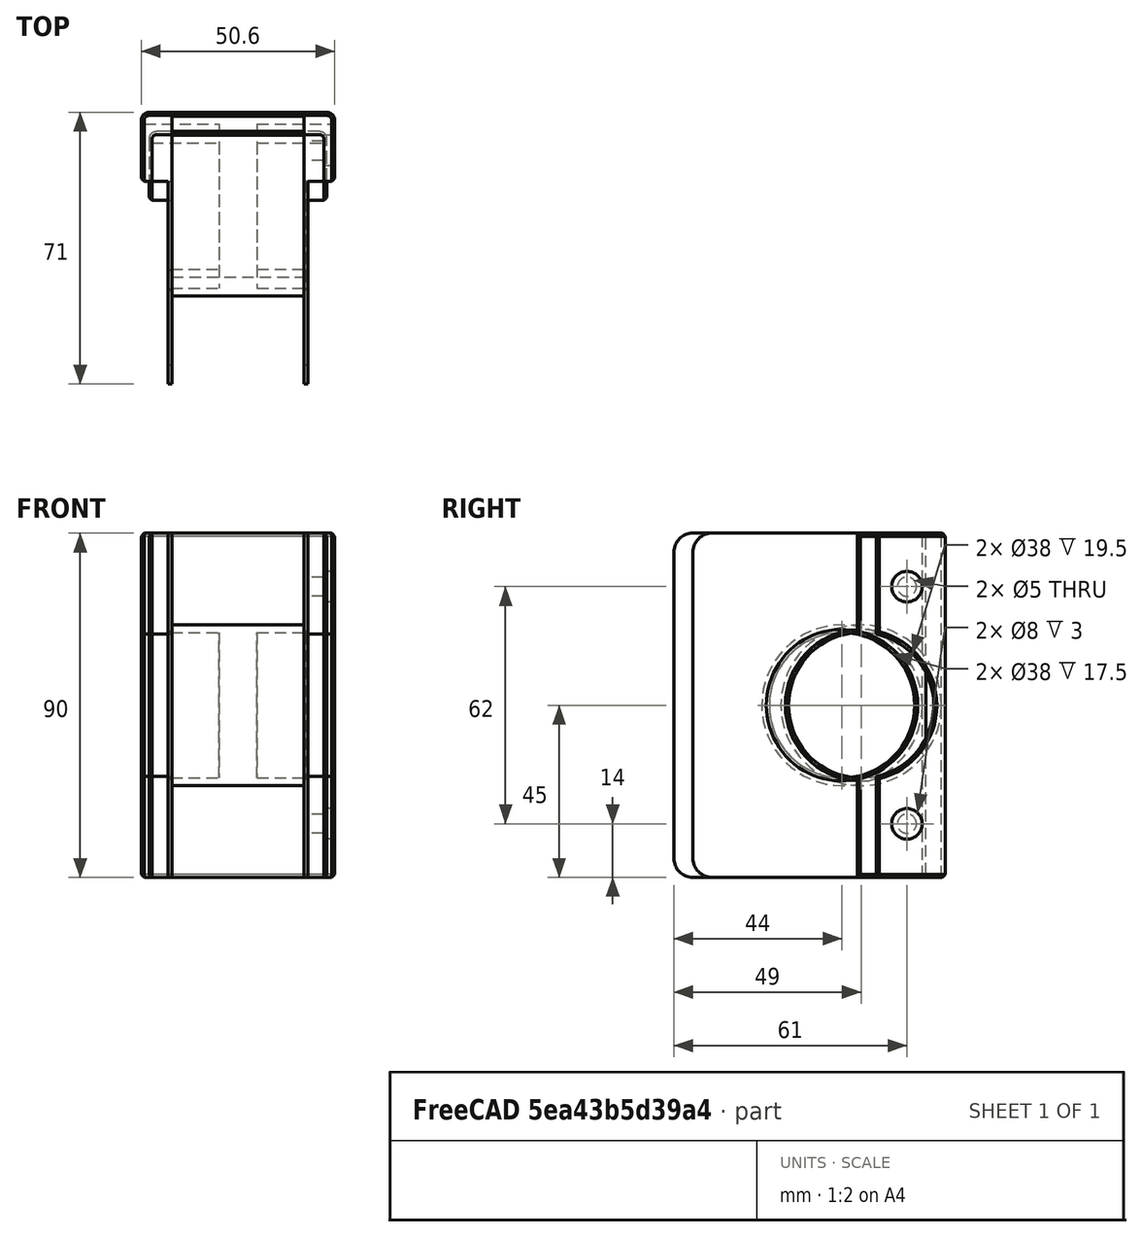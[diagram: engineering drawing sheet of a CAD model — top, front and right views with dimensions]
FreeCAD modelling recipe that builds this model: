
FCSTD DOCUMENT  (FreeCAD 1.1R39315 (Git))
Label: pocket door handle
License: All rights reserved
LicenseURL: http://en.wikipedia.org/wiki/All_rights_reserved
objects: Sketcher::SketchObject×9, PartDesign::Pad×6, PartDesign::Fillet×4, PartDesign::Pocket×3, PartDesign::Chamfer×2, PartDesign::Body×2, PartDesign::Hole×1
note: 68 computed .brp shape members not serialized (recipe doc carries the construction recipe); baked Part::Feature solids carry a one-line shape summary decoded from their .brp

FEATURE [Sketcher::SketchObject] Sketch
  ArcFitTolerance = 0
  AttachmentSupport = -> [XY_Plane]
  FullyConstrained = true
  MakeInternals = false
  MapMode = 5
  sketch-geometry (12):
    g0: LineSegment StartX=-17.3 StartY=-30 StartZ=0 EndX=-17.3 EndY=30 EndZ=0
    g1: LineSegment StartX=-17.3 StartY=30 StartZ=0 EndX=17.3 EndY=30 EndZ=0
    g2: LineSegment StartX=17.3 StartY=30 StartZ=0 EndX=17.3 EndY=-30 EndZ=0
    g3: LineSegment StartX=17.3 StartY=-30 StartZ=0 EndX=18.3 EndY=-30 EndZ=0
    g4: LineSegment StartX=18.3 StartY=-30 StartZ=0 EndX=18.3 EndY=13 EndZ=0
    g5: LineSegment StartX=18.3 StartY=13 StartZ=0 EndX=23.3 EndY=13 EndZ=0
    g6: LineSegment StartX=23.3 StartY=13 StartZ=0 EndX=23.3 EndY=31 EndZ=0
    g7: LineSegment StartX=23.3 StartY=31 StartZ=0 EndX=-23.3 EndY=31 EndZ=0
    g8: LineSegment StartX=-23.3 StartY=31 StartZ=0 EndX=-23.3 EndY=13 EndZ=0
    g9: LineSegment StartX=-23.3 StartY=13 StartZ=0 EndX=-18.3 EndY=13 EndZ=0
    g10: LineSegment StartX=-18.3 StartY=13 StartZ=0 EndX=-18.3 EndY=-30 EndZ=0
    g11: LineSegment StartX=-18.3 StartY=-30 StartZ=0 EndX=-17.3 EndY=-30 EndZ=0
  constraints (34):
    c: Vertical(g0)
    c: Coincident(g0,g1)
    c: Horizontal(g1)
    c: Coincident(g1,g2)
    c: Coincident(g2,g3)
    c: Horizontal(g3)
    c: Coincident(g3,g4)
    c: Vertical(g4)
    c: Coincident(g4,g5)
    c: Horizontal(g5)
    c: Coincident(g5,g6)
    c: Vertical(g6)
    c: Coincident(g6,g7)
    c: Horizontal(g7)
    c: Coincident(g7,g8)
    c: Vertical(g8)
    c: Coincident(g8,g9)
    c: Horizontal(g9)
    c: Coincident(g9,g10)
    c: Vertical(g10)
    c: Coincident(g10,g11)
    c: Coincident(g11,g0)
    c: Horizontal(g11)
    c: Symmetric(g2,g0,g-2)
    c: Equal(g11,g3)
    c: Equal(g9,g5)
    c: Equal(g6,g8)
    c: DistanceY(g0,g7) = 1
    c: DistanceX(g9,g0) = 1
    c: DistanceY(g8,g8) = 18
    c: Symmetric(g0,g1,g-1)
    c: DistanceX(g1,g1) = 34.6
    c: DistanceY(g2,g2) = 60
    c: DistanceX(g9,g9) = 5
FEATURE [PartDesign::Pad] Pad
  Direction = (0,0,1)
  Length = 90
  Length2 = 10
  Profile = -> Sketch
  ReferenceAxis = -> Sketch [N_Axis]
  Suppressed = false
  Type = 0
FEATURE [Sketcher::SketchObject] Sketch001
  ArcFitTolerance = 0
  AttachmentSupport = -> [Pad]
  ExternalGeometry = -> [Pad]
  FullyConstrained = true
  MakeInternals = false
  MapMode = 5
  Placement = pos=(23.3,0,0) rot=(0.57735,0.57735,0.57735;2.0944rad)
  sketch-geometry (3):
    g0: Circle CenterX=9 CenterY=45 CenterZ=0 NormalX=0 NormalY=0 NormalZ=1 AngleXU=0 Radius=19
    g1: GeomPoint X=31 Y=45 Z=0
    g2: Circle CenterX=9 CenterY=45 CenterZ=0 NormalX=0 NormalY=0 NormalZ=1 AngleXU=0 Radius=21
  constraints (6):
    c: Diameter(g0) = 38
    c: DistanceX(g0,g-3) = 22
    c: Symmetric(g-3,g-3,g1)
    c: Horizontal(g0,g1)
    c: Coincident(g2,g0)
    c: Diameter(g2) = 42
FEATURE [PartDesign::Pocket] Pocket
  BaseFeature = -> Pad
  Direction = (-1,0,0)
  Length = 5
  Length2 = 5
  Profile = -> Sketch001 [Edge1]
  ReferenceAxis = -> Sketch001 [N_Axis]
  Suppressed = false
  Type = 1
FEATURE [Sketcher::SketchObject] Sketch002
  ArcFitTolerance = 0
  AttachmentSupport = -> [Pocket]
  ExternalGeometry = -> [Sketch001]
  FullyConstrained = true
  MakeInternals = false
  MapMode = 5
  Placement = pos=(18.3,0,0) rot=(0.57735,0.57735,0.57735;2.0944rad)
  sketch-geometry (2):
    g0: Circle CenterX=9 CenterY=45 CenterZ=0 NormalX=0 NormalY=0 NormalZ=1 AngleXU=0 Radius=19
    g1: Circle CenterX=9 CenterY=45 CenterZ=0 NormalX=0 NormalY=0 NormalZ=1 AngleXU=0 Radius=21
  constraints (4):
    c: Coincident(g0,g-4)
    c: Coincident(g1,g0)
    c: Equal(g1,g-4)
    c: Equal(g0,g-3)
FEATURE [PartDesign::Fillet] Fillet
  Base = -> Pocket [Edge46,Edge50]
  BaseFeature = -> Pocket
  Radius = 2
  SupportTransform = false
  Suppressed = false
  UseAllEdges = false
FEATURE [PartDesign::Pad] Pad001
  BaseFeature = -> Fillet
  Direction = (1,0,0)
  Length = 10
  Length2 = 10
  Profile = -> Sketch002
  ReferenceAxis = -> Sketch002 [N_Axis]
  Reversed = true
  Suppressed = false
  Type = 3
  UpToFace = -> Fillet [Face13]
FEATURE [Sketcher::SketchObject] Sketch003
  ArcFitTolerance = 0
  AttachmentSupport = -> [YZ_Plane]
  ExternalGeometry = -> [Pad001]
  FullyConstrained = true
  MakeInternals = false
  MapMode = 5
  Placement = pos=(0,0,0) rot=(0.57735,0.57735,0.57735;2.0944rad)
  sketch-geometry (1):
    g0: Circle CenterX=9 CenterY=45 CenterZ=0 NormalX=0 NormalY=0 NormalZ=1 AngleXU=0 Radius=21
  constraints (2):
    c: Coincident(g0,g-3)
    c: PointOnObject(g-3,g0)
FEATURE [PartDesign::Pad] Pad002
  BaseFeature = -> Pad001
  Direction = (1,0,0)
  Length = 10
  Length2 = 10
  Midplane = true
  Profile = -> Sketch003
  ReferenceAxis = -> Sketch003 [N_Axis]
  Refine = true
  Suppressed = false
  Type = 0
FEATURE [PartDesign::Chamfer] Chamfer
  Angle = 45
  Base = -> Pad002 [Edge36,Edge60,Edge8,Edge32,Edge35,Edge33,Edge18,Edge59,Edge19,Edge17,Edge1,Edge16]
  BaseFeature = -> Pad002
  ChamferType = 0
  FlipDirection = false
  Size = 0.8
  Size2 = 1
  SupportTransform = false
  Suppressed = false
  UseAllEdges = false
FEATURE [PartDesign::Fillet] Fillet001
  Base = -> Chamfer [Edge30,Edge53,Edge5,Edge13]
  BaseFeature = -> Chamfer
  Radius = 5
  SupportTransform = false
  Suppressed = false
  UseAllEdges = false
FEATURE [PartDesign::Body] Body
  AllowCompound = false
  Group = -> [Sketch,Pad,Sketch001,Pocket,Sketch002,Fillet,Pad001,Sketch003,Pad002,Chamfer,Fillet001]
  Origin = -> Origin
  Tip = -> Fillet001
FEATURE [Sketcher::SketchObject] Sketch004
  ArcFitTolerance = 0
  AttachmentSupport = -> [XY_Plane001]
  FullyConstrained = true
  MakeInternals = false
  MapMode = 5
  sketch-geometry (12):
    g0: LineSegment StartX=-17.3 StartY=-35 StartZ=0 EndX=-17.3 EndY=35 EndZ=0
    g1: LineSegment StartX=-17.3 StartY=35 StartZ=0 EndX=17.3 EndY=35 EndZ=0
    g2: LineSegment StartX=17.3 StartY=35 StartZ=0 EndX=17.3 EndY=-35 EndZ=0
    g3: LineSegment StartX=17.3 StartY=-35 StartZ=0 EndX=18.3 EndY=-35 EndZ=0
    g4: LineSegment StartX=18.3 StartY=-35 StartZ=0 EndX=18.3 EndY=18 EndZ=0
    g5: LineSegment StartX=18.3 StartY=18 StartZ=0 EndX=25.3 EndY=18 EndZ=0
    g6: LineSegment StartX=25.3 StartY=18 StartZ=0 EndX=25.3 EndY=36 EndZ=0
    g7: LineSegment StartX=25.3 StartY=36 StartZ=0 EndX=-25.3 EndY=36 EndZ=0
    g8: LineSegment StartX=-25.3 StartY=36 StartZ=0 EndX=-25.3 EndY=18 EndZ=0
    g9: LineSegment StartX=-25.3 StartY=18 StartZ=0 EndX=-18.3 EndY=18 EndZ=0
    g10: LineSegment StartX=-18.3 StartY=18 StartZ=0 EndX=-18.3 EndY=-35 EndZ=0
    g11: LineSegment StartX=-18.3 StartY=-35 StartZ=0 EndX=-17.3 EndY=-35 EndZ=0
  constraints (34):
    c: Vertical(g0)
    c: Coincident(g0,g1)
    c: Horizontal(g1)
    c: Coincident(g1,g2)
    c: Coincident(g2,g3)
    c: Horizontal(g3)
    c: Coincident(g3,g4)
    c: Vertical(g4)
    c: Coincident(g4,g5)
    c: Horizontal(g5)
    c: Coincident(g5,g6)
    c: Vertical(g6)
    c: Coincident(g6,g7)
    c: Horizontal(g7)
    c: Coincident(g7,g8)
    c: Vertical(g8)
    c: Coincident(g8,g9)
    c: Horizontal(g9)
    c: Coincident(g9,g10)
    c: Vertical(g10)
    c: Coincident(g10,g11)
    c: Coincident(g11,g0)
    c: Horizontal(g11)
    c: Symmetric(g2,g0,g-2)
    c: Equal(g11,g3)
    c: Equal(g9,g5)
    c: Equal(g6,g8)
    c: DistanceY(g0,g7) = 1
    c: DistanceX(g9,g0) = 1
    c: DistanceY(g8,g8) = 18
    c: Symmetric(g0,g1,g-1)
    c: DistanceX(g1,g1) = 34.6
    c: DistanceY(g2,g2) = 70
    c: DistanceX(g9,g9) = 7
FEATURE [PartDesign::Pad] Pad003
  Direction = (0,0,1)
  Length = 90
  Length2 = 10
  Profile = -> Sketch004
  ReferenceAxis = -> Sketch004 [N_Axis]
  Suppressed = false
  Type = 0
FEATURE [Sketcher::SketchObject] Sketch005
  ArcFitTolerance = 0
  AttachmentSupport = -> [Pad003]
  ExternalGeometry = -> [Pad003]
  FullyConstrained = true
  MakeInternals = false
  MapMode = 5
  Placement = pos=(25.3,0,0) rot=(0.57735,0.57735,0.57735;2.0944rad)
  sketch-geometry (3):
    g0: Circle CenterX=14 CenterY=45 CenterZ=0 NormalX=0 NormalY=0 NormalZ=1 AngleXU=0 Radius=19
    g1: GeomPoint X=36 Y=45 Z=0
    g2: Circle CenterX=14 CenterY=45 CenterZ=0 NormalX=0 NormalY=0 NormalZ=1 AngleXU=0 Radius=21
  constraints (6):
    c: Diameter(g0) = 38
    c: DistanceX(g0,g-3) = 22
    c: Symmetric(g-3,g-3,g1)
    c: Horizontal(g0,g1)
    c: Coincident(g2,g0)
    c: Diameter(g2) = 42
FEATURE [PartDesign::Pocket] Pocket001
  BaseFeature = -> Pad003
  Direction = (-1,0,0)
  Length = 5
  Length2 = 5
  Profile = -> Sketch005 [Edge1]
  ReferenceAxis = -> Sketch005 [N_Axis]
  Suppressed = false
  Type = 1
FEATURE [PartDesign::Fillet] Fillet002
  Base = -> Pocket001 [Edge46,Edge50]
  BaseFeature = -> Pocket001
  Radius = 2
  SupportTransform = false
  Suppressed = false
  UseAllEdges = false
FEATURE [Sketcher::SketchObject] Sketch006
  ArcFitTolerance = 0
  AttachmentSupport = -> [Pocket001]
  ExternalGeometry = -> [Sketch005]
  FullyConstrained = true
  MakeInternals = false
  MapMode = 5
  Placement = pos=(18.3,0,0) rot=(0.57735,0.57735,0.57735;2.0944rad)
  sketch-geometry (2):
    g0: Circle CenterX=14 CenterY=45 CenterZ=0 NormalX=0 NormalY=0 NormalZ=1 AngleXU=0 Radius=19
    g1: Circle CenterX=14 CenterY=45 CenterZ=0 NormalX=0 NormalY=0 NormalZ=1 AngleXU=0 Radius=21
  constraints (4):
    c: Coincident(g0,g-4)
    c: Coincident(g1,g0)
    c: Equal(g1,g-4)
    c: Equal(g0,g-3)
FEATURE [PartDesign::Pad] Pad004
  BaseFeature = -> Fillet002
  Direction = (1,0,0)
  Length = 10
  Length2 = 10
  Profile = -> Sketch006
  ReferenceAxis = -> Sketch006 [N_Axis]
  Reversed = true
  Suppressed = false
  Type = 3
  UpToFace = -> Fillet002 [Face13]
FEATURE [Sketcher::SketchObject] Sketch007
  ArcFitTolerance = 0
  AttachmentSupport = -> [YZ_Plane001]
  ExternalGeometry = -> [Pad004]
  FullyConstrained = true
  MakeInternals = false
  MapMode = 5
  Placement = pos=(0,0,0) rot=(0.57735,0.57735,0.57735;2.0944rad)
  sketch-geometry (1):
    g0: Circle CenterX=14 CenterY=45 CenterZ=0 NormalX=0 NormalY=0 NormalZ=1 AngleXU=0 Radius=21
  constraints (2):
    c: Coincident(g0,g-3)
    c: PointOnObject(g-3,g0)
FEATURE [PartDesign::Pad] Pad005
  BaseFeature = -> Pad004
  Direction = (1,0,0)
  Length = 10
  Length2 = 10
  Midplane = true
  Profile = -> Sketch007
  ReferenceAxis = -> Sketch007 [N_Axis]
  Refine = true
  Suppressed = false
  Type = 0
FEATURE [PartDesign::Chamfer] Chamfer001
  Angle = 45
  Base = -> Pad005 [Edge36,Edge60,Edge8,Edge32,Edge35,Edge33,Edge18,Edge59,Edge19,Edge17,Edge1,Edge16]
  BaseFeature = -> Pad005
  ChamferType = 0
  FlipDirection = false
  Size = 0.8
  Size2 = 1
  SupportTransform = false
  Suppressed = false
  UseAllEdges = false
FEATURE [PartDesign::Fillet] Fillet003
  Base = -> Chamfer001 [Edge30,Edge53,Edge5,Edge13]
  BaseFeature = -> Chamfer001
  Radius = 5
  SupportTransform = false
  Suppressed = false
  UseAllEdges = false
FEATURE [Sketcher::SketchObject] Sketch008
  ArcFitTolerance = 1e-06
  AttachmentSupport = -> [Fillet003]
  ExternalGeometry = -> [Fillet003]
  FullyConstrained = true
  MakeInternals = false
  MapMode = 5
  Placement = pos=(25.3,0,0) rot=(0.57735,0.57735,0.57735;2.0944rad)
  sketch-geometry (4):
    g0: GeomPoint [constr] X=26 Y=0 Z=0
    g1: GeomPoint [constr] X=26 Y=90 Z=0
    g2: Circle CenterX=26 CenterY=76 CenterZ=0 NormalX=0 NormalY=0 NormalZ=1 AngleXU=0 Radius=2
    g3: Circle CenterX=26 CenterY=14 CenterZ=0 NormalX=0 NormalY=0 NormalZ=1 AngleXU=0 Radius=2
  constraints (8):
    c: Symmetric(g-4,g-4,g0)
    c: Symmetric(g-3,g-3,g1)
    c: Vertical(g0,g3)
    c: Vertical(g2,g3)
    c: DistanceY(g-4,g3) = 14
    c: DistanceY(g2,g-3) = 14
    c: Equal(g2,g3)
    c: Diameter(g2) = 4
FEATURE [PartDesign::Pocket] Pocket002
  BaseFeature = -> Fillet003
  Direction = (-1,0,0)
  Length = 0
  Length2 = 5
  Profile = -> Sketch008
  ReferenceAxis = -> Sketch008 [N_Axis]
  Refine = true
  Suppressed = false
  Type = 3
  UpToFace = -> Fillet003 [Face5]
FEATURE [PartDesign::Hole] Hole
  BaseFeature = -> Pocket002
  CustomThreadClearance = 0
  Depth = 25
  DepthType = 0
  Diameter = 5
  DrillForDepth = false
  DrillPoint = 1
  DrillPointAngle = 118
  HoleCutCountersinkAngle = 90
  HoleCutCustomValues = false
  HoleCutDepth = 3
  HoleCutDiameter = 8
  HoleCutType = 1
  ModelThread = false
  Profile = -> Pocket002 [Edge89,Edge91]
  Refine = true
  Suppressed = false
  Tapered = false
  TaperedAngle = 90
  ThreadClass = 0
  ThreadDepth = 25
  ThreadDepthType = 0
  ThreadDirection = 0
  ThreadFit = 0
  ThreadSize = 6
  ThreadType = 3
  Threaded = false
  UseCustomThreadClearance = false
FEATURE [PartDesign::Body] Body001
  AllowCompound = false
  Group = -> [Sketch004,Pad003,Sketch005,Pocket001,Sketch006,Fillet002,Pad004,Sketch007,Pad005,Chamfer001,Fillet003,Sketch008,Pocket002,Hole]
  Origin = -> Origin001
  Tip = -> Hole
